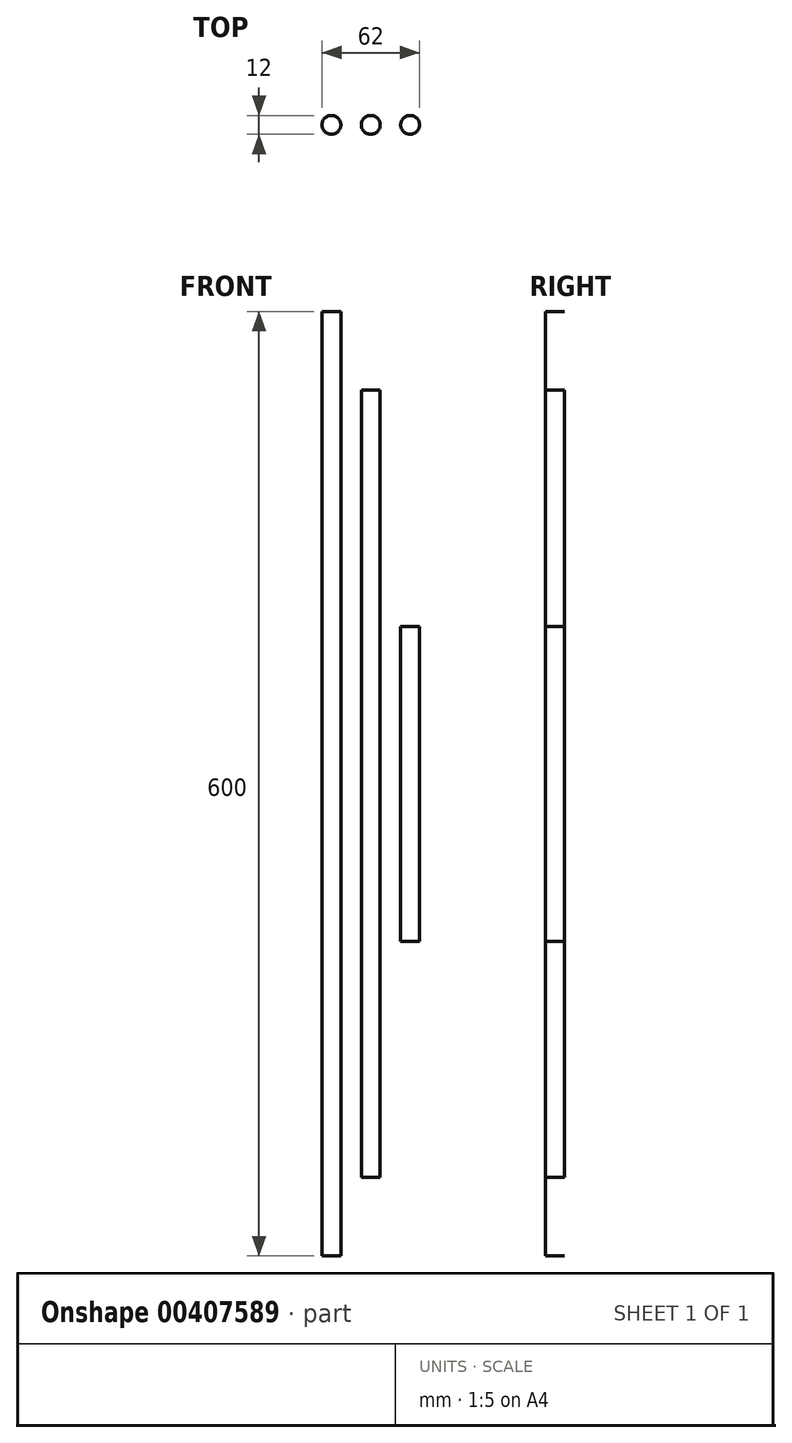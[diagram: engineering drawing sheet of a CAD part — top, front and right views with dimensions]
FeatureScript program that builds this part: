
annotation { "Feature Type Name" : "Feature", "Feature Type Description" : "" }
export const myFeature = defineFeature(function(context is Context, id is Id, definition is map)
    precondition{}
    {
        {
            assignVariable(context, id + "F0", {"name" : "xg", "anyValue" : 500});
        }
        {
            assignVariable(context, id + "F1", {"name" : "yg", "anyValue" : 600});
        }
        {
            assignVariable(context, id + "F2", {"name" : "zg", "anyValue" : 200});
        }
        {
            var Q0;
            Q0=qCreatedBy(makeId("Top.planeOp"),FACE);
            var sketch = newSketch(context, id + "F3", { "sketchPlane" : qUnion([Q0])});
            skLineSegment(sketch, "E0", {"start": v(-25, 0) * mm, "end": v(25, 0) * mm, "construction": true});
            skCircle(sketch, "E1", {"center": v(-25, 0) * mm, "radius": 6 * mm});
            skCircle(sketch, "E2", {"center": v(0, 0) * mm, "radius": 6 * mm});
            skCircle(sketch, "E3", {"center": v(25, 0) * mm, "radius": 6 * mm});
            skSolve(sketch);
        }
        {
            var Q0;
            Q0=makeQuery(id+"F3.imprint","IMPRINT",FACE,{"disambiguationData":[TD([[makeQuery(id+"F3.imprint","IMPRINT",EDGE,{"derivedFrom":sQuery(id+"F3.wireOp",EDGE,"E1")}),1.0]])]});
            extrude(context, id + "F4", {"entities" : qUnion([Q0]), "depth" : (getVariable(context, 'yg')) * mm, "symmetric" : true});
        }
        {
            var Q0;
            Q0=makeQuery(id+"F3.imprint","IMPRINT",FACE,{"disambiguationData":[TD([[makeQuery(id+"F3.imprint","IMPRINT",EDGE,{"derivedFrom":sQuery(id+"F3.wireOp",EDGE,"E2")}),1.0]])]});
            extrude(context, id + "F5", {"entities" : qUnion([Q0]), "depth" : (getVariable(context, 'xg')) * mm, "symmetric" : true});
        }
        {
            var Q0;
            Q0=makeQuery(id+"F3.imprint","IMPRINT",FACE,{"disambiguationData":[TD([[makeQuery(id+"F3.imprint","IMPRINT",EDGE,{"derivedFrom":sQuery(id+"F3.wireOp",EDGE,"E3")}),1.0]])]});
            extrude(context, id + "F6", {"entities" : qUnion([Q0]), "depth" : (getVariable(context, 'zg')) * mm, "symmetric" : true});
        }
    });
